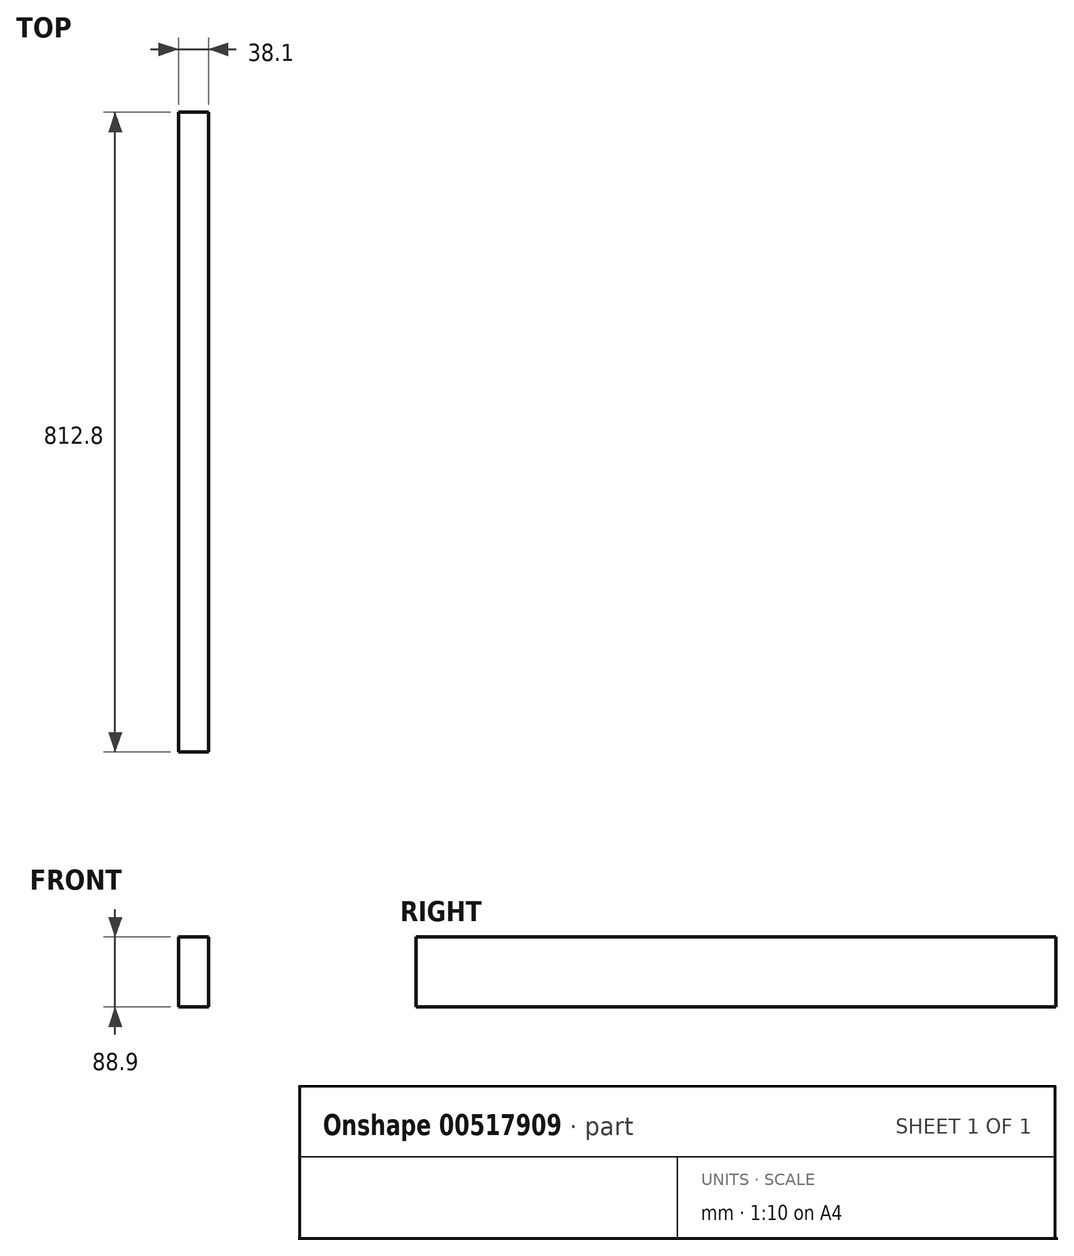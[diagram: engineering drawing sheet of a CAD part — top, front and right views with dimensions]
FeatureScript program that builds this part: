
annotation { "Feature Type Name" : "Feature", "Feature Type Description" : "" }
export const myFeature = defineFeature(function(context is Context, id is Id, definition is map)
    precondition{}
    {
        {
            var Q0;
            Q0=qCreatedBy(makeId("Front.planeOp"),FACE);
            var sketch = newSketch(context, id + "F0", { "sketchPlane" : qUnion([Q0])});
            skLineSegment(sketch, "E0.bottom", {"start": v(19.05, 44.45) * mm, "end": v(-19.05, 44.45) * mm});
            skLineSegment(sketch, "E0.top", {"start": v(19.05, -44.45) * mm, "end": v(-19.05, -44.45) * mm});
            skLineSegment(sketch, "E0.left", {"start": v(19.05, 44.45) * mm, "end": v(19.05, -44.45) * mm});
            skLineSegment(sketch, "E0.right", {"start": v(-19.05, 44.45) * mm, "end": v(-19.05, -44.45) * mm});
            skPoint(sketch, "E0.middle", {"position": v(0, 0) * mm});
            skSolve(sketch);
        }
        {
            var Q0;
            Q0=makeQuery(id+"F0.imprint","IMPRINT",FACE,{"disambiguationData":[TD([[makeQuery(id+"F0.imprint","IMPRINT",EDGE,{"derivedFrom":sQuery(id+"F0.wireOp",EDGE,"E0.bottom")}),1.0]])]});
            extrude(context, id + "F1", {"entities" : qUnion([Q0]), "endBound" : BoundingType.SYMMETRIC, "depth" : 812.8 * mm, "offsetDistance" : 25.4 * mm});
        }
    });
